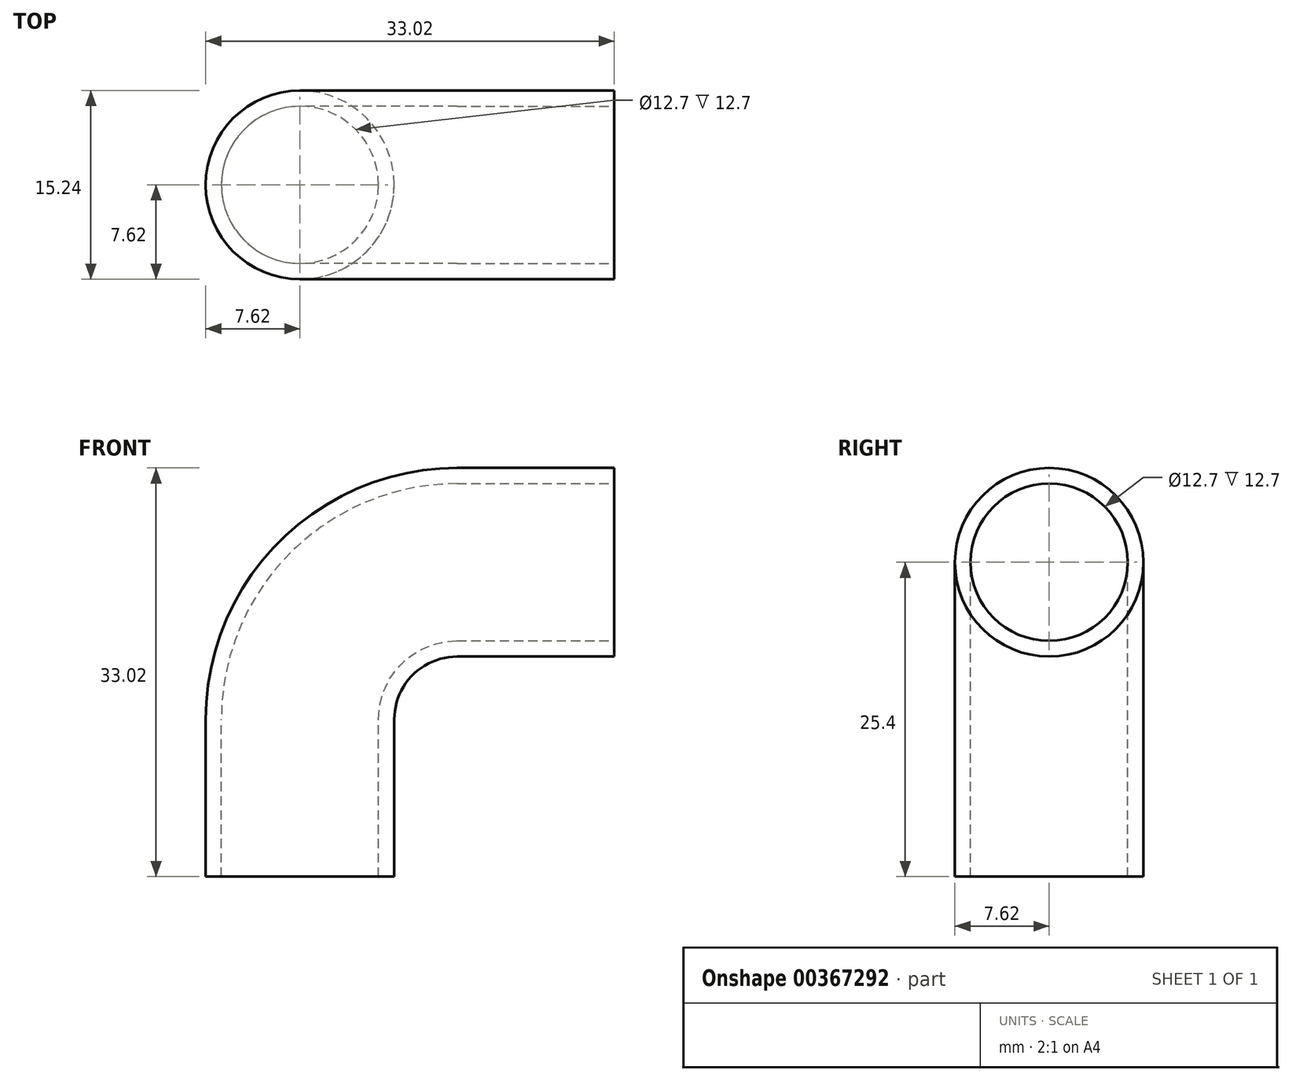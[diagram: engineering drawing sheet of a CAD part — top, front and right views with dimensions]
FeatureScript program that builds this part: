
annotation { "Feature Type Name" : "Feature", "Feature Type Description" : "" }
export const myFeature = defineFeature(function(context is Context, id is Id, definition is map)
    precondition{}
    {
        {
            var Q0;
            Q0=qCreatedBy(makeId("Top.planeOp"),FACE);
            var sketch = newSketch(context, id + "F0", { "sketchPlane" : qUnion([Q0])});
            skCircle(sketch, "E0", {"center": v(0, 0) * mm, "radius": 6.35 * mm});
            skCircle(sketch, "E1", {"center": v(0, 0) * mm, "radius": 7.62 * mm});
            skSolve(sketch);
        }
        {
            var Q0;
            Q0=qCreatedBy(makeId("Front.planeOp"),FACE);
            var sketch = newSketch(context, id + "F1", { "sketchPlane" : qUnion([Q0])});
            skLineSegment(sketch, "E2", {"start": v(0, 0) * mm, "end": v(0, 12.7) * mm});
            skLineSegment(sketch, "E3", {"start": v(12.7, 25.4) * mm, "end": v(25.4, 25.4) * mm});
            skPoint(sketch, "E4.visualSharp", {"position": v(0, 25.4) * mm});
            skArc(sketch, "E4.filletArc", {"start": v(12.7, 25.4) * mm, "mid": v(3.72, 21.68) * mm, "end": v(0, 12.7) * mm});
            skSolve(sketch);
        }
        {
            var Q0;
            Q0=qSketchRegion(id+"F0",true);
            var Q1;
            Q1=qConstructionFilter(qBodyType(qCreatedBy(id+"F1",EDGE),BodyType.WIRE),ConstructionObject.NO);
            sweep(context, id + "F2", {"profiles" : qUnion([Q0]), "path" : qUnion([Q1])});
        }
    });
